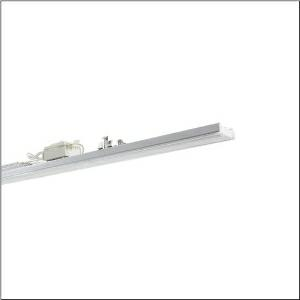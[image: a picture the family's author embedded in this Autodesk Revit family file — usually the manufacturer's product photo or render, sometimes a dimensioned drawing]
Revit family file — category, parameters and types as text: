
# Revit family: licross_21_recessed_mo_52tl19cn185g
name_source: partatom
category: Lighting Fixtures
units: mm (PartAtom-declared; Revit-internal decimal feet)

## family parameters
Cut with Voids When Loaded = No
Host = Face
Light Source = No
Part Type = Normal
Room Calculation Point = No
Round Connector Dimension = Use Diameter
Shared = No

## types (1)
- --- (1 x LED, 8590 lm, 49.9 W, 3500K)
    Apparent Load = 50 VA
    CIE Flux Codes = 55 90 98 100 100
    Color Rendering = 80
    Color Temperature = 3500K
    Default Elevation = 1800 mm
    Description = Licross 21 Recessed MO, luminaire insert, of sheet steel, galvanised, coil coated, white, length: 1.500mm, width: 66mm, height: 67mm, LED rated luminous flux: 8.590lm, light colour: 835, SDCM (Standard Deviation of Colour Matching)MacAdam ≤ 3 SDCM (initial), control gear: ON/OFF Multilumen, CLOi, with plug, 3-pole, with phase selection, mains connection: 220..240V, AC, 50/60Hz, start of lifetime: 50W, end of service life: 61W, internal wiring halogen-free, primary light control with lens, of plastic, primary optical cover: cover, of PMMA, light emission: direct distribution, primary light characteristic: double asymmetric, protection rating (complete): IP40, insulation class (complete): insulation class I (protective earthing), certification: CE, ENEC, VDE, UKCA, protection symbol: D if used in an environment without relevant dust loads with corresponding accessories, impact resistance: IK06, permissible ambient temperature for indoor applications: -35..+35°C, corresponds to IFS (International Featured Standards) requirements for safety and quality in the food industry, reducing of maximum allowable ambient temperature of 5°C with ceiling mounting, LABS conformity tested according to VDMA 24364:2018-05, The light source and the operating device comply with the requirements of the Ecodesign Regulation (EU) 2019/2020 and are replaceable in accordance with this regulation, packaging unit: 1 piece
    Height = 58 mm
    Lamp = 1 x LED
    Lamp Light Flux = 8590 lm
    Lamp Power = 49.9 W
    Lamp count = 1
    Length = 1500 mm
    Luminous efficacy = 172 lm/W
    Manufacturer = Siteco
    ModVariant = No
    Model = 52TL19CN185G
    Mounting Place = Ceiling
    Mounting Type = Pendant
    Number of Poles = 1
    OnlyDefault = Yes
    Power Factor = 1
    Product Name = Licross 21 Recessed MO
    Product group = luminaire insert | ceiling pendant
    ProductGroupID = 901
    Protection Class = Protection class I
    Protection Degree = IP 40
    RLX_Detail_Level = 1
    RLX_Emergency_Light_Flux = 0 lm
    RLX_Emergency_Type = 0
    RLX_Emergency_Type_DB = No
    RlxData = <blob elided: 22565 chars, md5=0a13d6ee>
    Socket = socket
    Standby Power = 0 W
    System Light Flux = 8590 lm
    System Power = 50 W
    Type Comments = factory setting: luminous flux: 100 % | (A | C | E) | 116 mA
    Type Image = l_1296930.jpg
    URL = http://relux.com
    VarID = @adj_075665
    Voltage = 0 V
    Weight = 0.00 kg
    Width = 66 mm

## geometry (parser evidence)
native form markers: Blend x4, Sweep x11
no freeform markers — native parametric forms only
